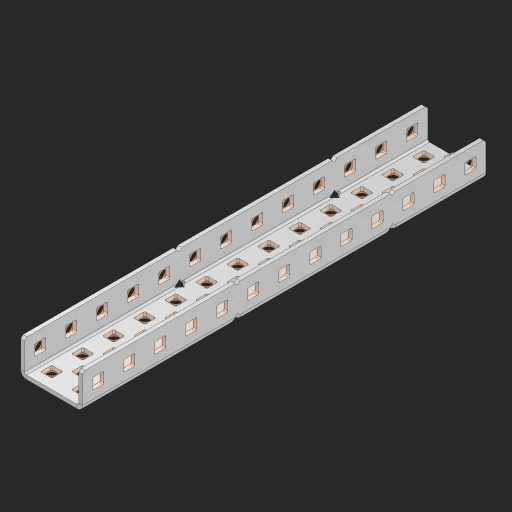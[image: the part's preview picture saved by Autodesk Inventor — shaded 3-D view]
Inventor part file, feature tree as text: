
AUTODESK INVENTOR PART (.ipt)
format: ipt  version: 2023 (Build 270158000, 158)  size: 1,079,296 bytes
history: native  units: in
note: dims shown in document units (in); Inventor stores cm internally (conversion verified against a paired STEP export)
features: other x72, extrude x63, sheet_metal_op x11, sketch x10, pattern_linear x2, mirror x1, chamfer x1
ambient origin geometry x8: Origin, YZ Plane, XZ Plane, XY Plane, X Axis, Y Axis, Z Axis, Center Point
bodies: Solid1 (feature_tree), Body (feature_tree)
feature tree (160):
  sheet_metal_op  "Flanges"
  other  "Flange Pattern Plane"
  other  "Flange Pattern Sketch"
  sheet_metal_op  "Flange Pattern"
  sheet_metal_op  "Body Pattern"
  pattern_linear  "Center Pattern"  Spacing1=0.0625in  [1 undecoded]
  other  "Arc Length"
  mirror  "Notch Mirror"
  pattern_linear  "Notch Pattern"  Spacing1=0.182in  [1 undecoded]
  chamfer  "End Chamfer"
  extrude  "Half Cut"  Depth=0.02in
  sketch  "Sketch1"  dims[d0=1.0in]
  other  "Plate1"
  sketch  "Sketch2"  dims[d1=6.5in]
  other  "Plate2"
  sheet_metal_op  "Bend1"
  sheet_metal_op  "Corner1"
  sketch  "Sketch3"  dims[d2=0.0625in]
  sketch  "Sketch7"  dims[d3=0.0625in]
  other  "Srf1"
  other  "Srf2"
  sketch  "Sketch8"  dims[d4=0.0312in]
  sketch  "Sketch9"  dims[d5=0.125in]
  other  "Srf91"
  sheet_metal_op  "Body Pattern Sketch"
  other  "Srf92"
  sketch  "Sketch13"  dims[d6=0.0625in]
  sketch  "Sketch14"  dims[d7=0.5in d8=90.0deg d9=0.0312in]
  sketch  "Sketch15"  dims[d10=0.25in]
  sketch  "Sketch16"  dims[d11=0.0625in d12=0.0625in d16=0.182in d17=0.02in d18=0.0625in d19=0.0in d20=0.25in d21=0.25in d38=5.1181in d40=0.5in d41=0.7874in d43=1.0in d46=0.172in d47=1.0in d48=0.0in d49=0.182in d50=0.02in d51=0.25in d52=0.25in d53=0.0625in d54=0.0in d55=0.172in d56=1.0in d57=0.0in d58=0.25in d60=5.1181in d62=0.5in d63=0.7874in d65=0.5in d85=0.1473in d86=0.1782in d88=0.04in d89=0.0625in d90=0.0in d91=0.04in d92=0.0491in d95=2.5in d96=0.04in d97=0.25in d98=45.0deg d99=0.25in d100=0.5in d101=0.0in d102=2.497in d106=0.182in d107=0.02in d108=0.5in d109=0.5in d110=0.0625in d111=0.0in d112=0.172in d113=0.5in d114=0.0in d117=0.5in d118=0.5in d119=0.5in]
  other  "Srf786"
  other  "Srf823"
  other  "Srf824"
  other  "Srf825"
  other  "Srf826"
  other  "Srf827"
  other  "Srf828"
  other  "Srf829"
  other  "Srf856"
  other  "Srf857"
  other  "Srf858"
  other  "Srf859"
  other  "Srf860"
  other  "Srf861"
  other  "Srf862"
  other  "Srf889"
  other  "Srf890"
  other  "Srf891"
  other  "Srf892"
  other  "Srf893"
  other  "Srf894"
  other  "Srf895"
  other  "Srf896"
  other  "Srf922"
  other  "Srf923"
  other  "Srf924"
  other  "Srf925"
  other  "Srf926"
  other  "Srf959"
  other  "Srf960"
  other  "Srf961"
  other  "Srf962"
  other  "Srf963"
  other  "Srf996"
  other  "Srf997"
  other  "Srf998"
  other  "Srf999"
  other  "Srf1143"
  other  "Srf1144"
  other  "Srf1145"
  other  "Srf1146"
  other  "Srf1147"
  other  "Srf1148"
  other  "Srf1149"
  other  "Srf1150"
  other  "Srf1151"
  other  "Srf1152"
  other  "Srf1153"
  other  "Srf1154"
  other  "Srf1199"
  other  "Srf1200"
  other  "Srf1201"
  other  "Srf1202"
  other  "Srf1203"
  other  "Srf1204"
  other  "Srf1205"
  other  "Srf1206"
  other  "Srf1207"
  other  "Srf1208"
  other  "Srf1209"
  other  "Srf1210"
  sheet_metal_op  "Flange Stamp"
  sheet_metal_op  "Flange Circle"
  sheet_metal_op  "Body Stamp"
  sheet_metal_op  "Body Circle"
  other  "Center Stamp"
  other  "Center Circle"
  sheet_metal_op  "Notch"
  extrude  "ExtrusionSrf2"  Depth=0.0625in
  extrude  "ExtrusionSrf92"  TaperAngle=0.0deg  [1 undecoded]
  extrude  "ExtrusionSrf823"  Depth=0.5in
  extrude  "ExtrusionSrf824"  Depth=0.5in
  extrude  "ExtrusionSrf825"  Depth=0.5in
  extrude  "ExtrusionSrf826"  Depth=0.5in
  extrude  "ExtrusionSrf827"  Depth=1.0in TaperAngle=0.0deg
  extrude  "ExtrusionSrf828"  Depth=0.5in
  extrude  "ExtrusionSrf829"  Depth=0.02in
  extrude  "ExtrusionSrf856"  Depth=0.5in
  extrude  "ExtrusionSrf857"  Depth=0.5in
  extrude  "ExtrusionSrf858"  Depth=0.0625in
  extrude  "ExtrusionSrf859"  TaperAngle=0.0deg  [1 undecoded]
  extrude  "ExtrusionSrf860"  Depth=0.5in
  extrude  "ExtrusionSrf861"  Depth=1.0in TaperAngle=0.0deg
  extrude  "ExtrusionSrf862"  Depth=0.5in
  extrude  "ExtrusionSrf889"  Depth=0.5in
  extrude  "ExtrusionSrf890"  Depth=0.5in
  extrude  "ExtrusionSrf891"  Depth=0.5in
  extrude  "ExtrusionSrf892"  Depth=0.5in
  extrude  "ExtrusionSrf893"  Depth=0.5in
  extrude  "ExtrusionSrf894"  Depth=0.0625in
  extrude  "ExtrusionSrf895"  TaperAngle=0.0deg  [1 undecoded]
  extrude  "ExtrusionSrf896"  Depth=0.5in
  extrude  "ExtrusionSrf922"  Depth=0.5in
  extrude  "ExtrusionSrf923"  Depth=2.5in
  extrude  "ExtrusionSrf924"  Depth=0.5in TaperAngle=45.0deg
  extrude  "ExtrusionSrf925"  Depth=0.5in
  extrude  "ExtrusionSrf926"  Depth=0.5in TaperAngle=0.0deg
  extrude  "ExtrusionSrf959"  Depth=0.5in
  extrude  "ExtrusionSrf960"  Depth=0.5in
  extrude  "ExtrusionSrf961"  Depth=0.02in
  extrude  "ExtrusionSrf962"  Depth=0.5in
  extrude  "ExtrusionSrf963"  Depth=0.5in
  extrude  "ExtrusionSrf996"  Depth=0.0625in
  extrude  "ExtrusionSrf997"  TaperAngle=0.0deg  [1 undecoded]
  extrude  "ExtrusionSrf998"  Depth=0.5in
  extrude  "ExtrusionSrf999"  Depth=0.5in TaperAngle=0.0deg
  extrude  "ExtrusionSrf1143"  Depth=0.5in
  extrude  "ExtrusionSrf1144"  Depth=0.5in
  extrude  "ExtrusionSrf1145"  Depth=0.5in
  extrude  "ExtrusionSrf1146"  [1 undecoded]
  extrude  "ExtrusionSrf1147"  [1 undecoded]
  extrude  "ExtrusionSrf1148"  [1 undecoded]
  extrude  "ExtrusionSrf1149"  [1 undecoded]
  extrude  "ExtrusionSrf1150"  [1 undecoded]
  extrude  "ExtrusionSrf1151"  [1 undecoded]
  extrude  "ExtrusionSrf1152"  [1 undecoded]
  extrude  "ExtrusionSrf1153"  [1 undecoded]
  extrude  "ExtrusionSrf1154"  [1 undecoded]
  extrude  "ExtrusionSrf1199"  [1 undecoded]
  extrude  "ExtrusionSrf1200"  [1 undecoded]
  extrude  "ExtrusionSrf1201"  [1 undecoded]
  extrude  "ExtrusionSrf1202"  [1 undecoded]
  extrude  "ExtrusionSrf1203"  [1 undecoded]
  extrude  "ExtrusionSrf1204"  [1 undecoded]
  extrude  "ExtrusionSrf1205"  [1 undecoded]
  extrude  "ExtrusionSrf1206"  [1 undecoded]
  extrude  "ExtrusionSrf1207"  [1 undecoded]
  extrude  "ExtrusionSrf1208"  [1 undecoded]
  extrude  "ExtrusionSrf1209"  [1 undecoded]
  extrude  "ExtrusionSrf1210"  [1 undecoded]
note: 27 required parameter values undecoded (feature->parameter linkage not recoverable at this tier; creation-order binding heuristic only, values carry confidence <= 0.55)
